# Revit family: BIM_RGV_INFINITY_F4_DN350-DN600_PFA16 PN10_PN16_HDW
name_source: partatom
category: Generic Models
revit_build: Autodesk Revit 2017 (Build: 20160225_1515(x64)
units: mm (PartAtom-declared; Revit-internal decimal feet)

## family parameters
Always vertical = Yes
Can host rebar = No
Cut with Voids When Loaded = No
Part Type = Normal
Room Calculation Point = No
Round Connector Dimension = Use Diameter
Shared = No
Work Plane-Based = No

## types (5) — shared parameters

## per-type parameters (varying)
| type | Nominal_Dia |
| DN350_PN10-16 | 350 mm  [stored 1.14829 ft] |
| DN400_PN10-16 | 400 mm  [stored 1.31234 ft] |
| DN450_PN10-16 | 450 mm  [stored 1.47638 ft] |
| DN500_PN10-16 | 500 mm  [stored 1.64042 ft] |
| DN600_PN10-16 | 600 mm |

type visibility flags: 5 boolean params named "<type name>" — each type sets only its own to Yes (folded from table)

note: [stored X ft] marks values corroborated as IEEE doubles in the binary element streams (Revit-internal decimal feet)

## geometry (parser evidence)
native form markers: Sweep x119
no freeform markers — native parametric forms only
